# Revit family: Domotics-SerieCivili-GEWISS-27COMBI_SYSTEM-IP55_LAMPEGGIATORI
name_source: partatom
category: Apparecchi elettrici
revit_build: Autodesk Revit 2016 (Build: 20161004_0715(x64)
units: mm (PartAtom-declared; Revit-internal decimal feet)

## family parameters
Condiviso = No
Host = Muro
Mantenere orientamento annotazione = No
Numero OmniClass = 23.80.50.00
Punto di calcolo locali = No
Quota connettore circolare = Usa diametro
Sempre verticale = Sì
Taglio con vuoti quando caricato = No
Tipo di parte = Normale
Titolo OmniClass = Terminals for Power Supply

## types (4) — shared parameters
Catalogo = DOMOTICS
Catalogo Serie = 27COMBI
Classe isolamento = II
Codice Electrocod = 0132
Colore = Grigio RAL 7035
Colore diffusore = GEWISS VETRINO GIALLO
Dim. esterne BxHxP (mm) = 66x82x95
Frequenza lampi = 1HZ
Glow Wire Test = 650°C
Grado di protezione = IP55
IDF = da7396fb-6b8b-4c5f-8f06-fa5cc08947e9
IDT = 642694f6-aaf2-4b3c-9aa4-08d332f019c7
Immagine tipo = GW27424.jpg
NUMERO DI POLI = 1
Norma di riferimento = EN 60598-1
Portalampada tipo = E14
Potenza = Max 25 W
Produttore = GEWISS S.p.A.
Scheda Tecnica = https://www.gewiss.com
Temperatura di installazione = -25 +60 °C
Termopressione con biglia = 70 °C
URL = https://www.gewiss.com
Versione file RFA = 18.0

## per-type parameters (varying)
| type | Codice EAN | Colore del diffusore | Descrizione | Modello | Tensione nominale |
| GW27424 - Lampeggiatore elettronico diffusore giallo 230V | 8011564056251 | Giallo | LAMPEGGIATORE ELETTR.DIF.GIALLO 230V | GW27424 | 230 V ac |
| GW27423 - Lampeggiatore elettronico diffusore giallo 24V | 8011564056244 | Giallo | LAMPEGGIATORE ELETTR.DIF.GIALLO 24V | GW27423 | 24 V ac |
| GW27421 - Lampeggiatore elettronico diffusore rosso 24V | 8011564056220 | Rosso | LAMPEGGIATORE ELETTR.DIF.ROSSO 24V | GW27421 | 24 V ac |
| GW27422 - Lampeggiatore elettronico diffusore rosso 230V | 8011564056237 | Rosso | LAMPEGGIATORE ELETTR.DIF.ROSSO 230V | GW27422 | 230 V ac |
